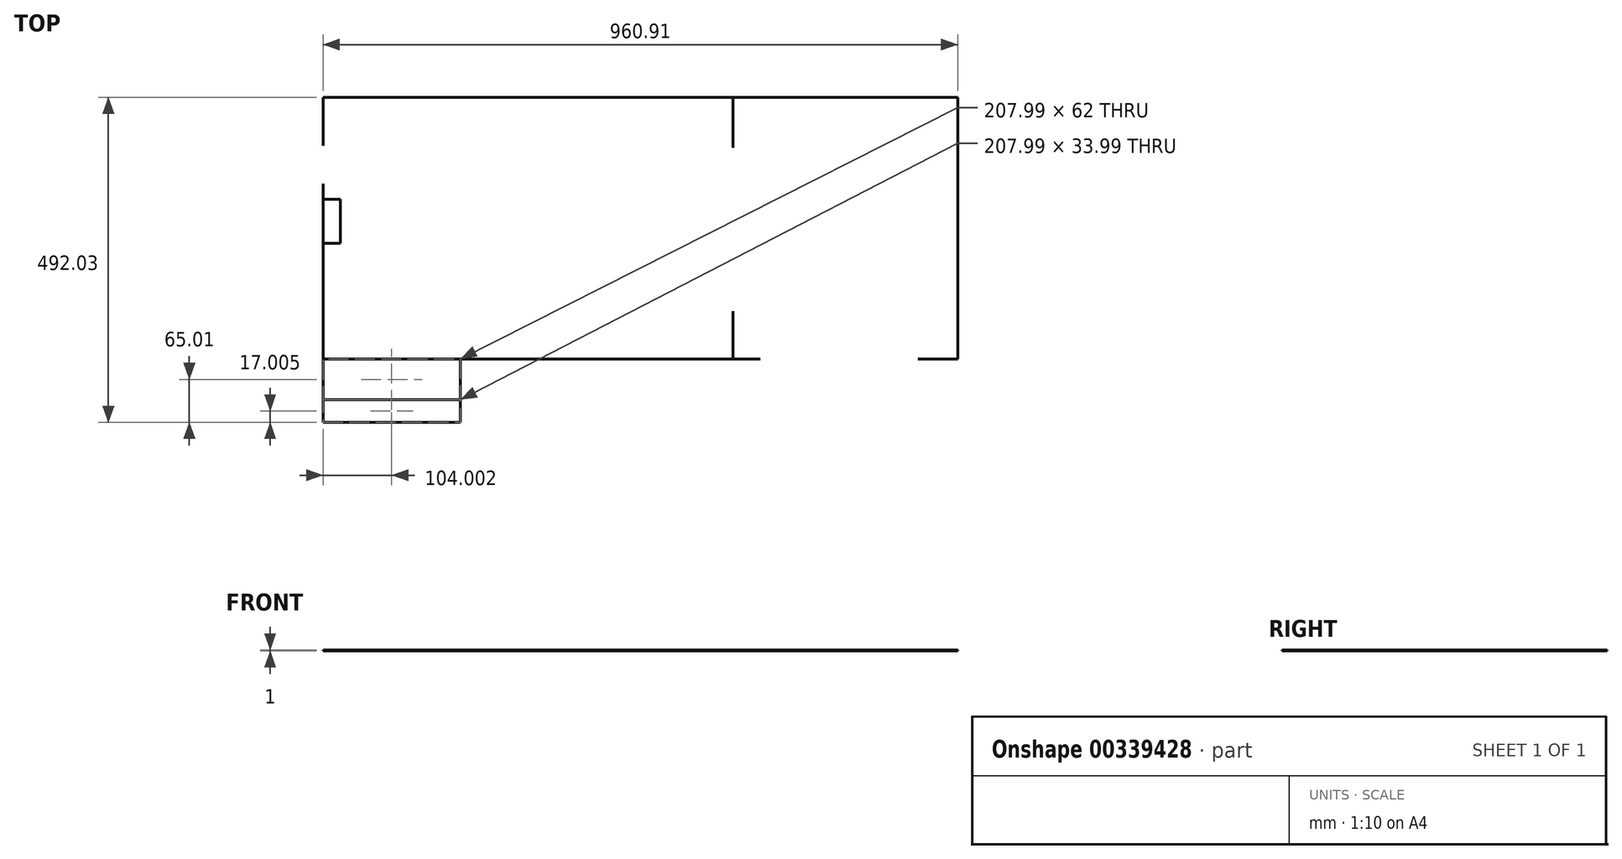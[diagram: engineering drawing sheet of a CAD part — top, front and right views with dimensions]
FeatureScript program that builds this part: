
annotation { "Feature Type Name" : "Feature", "Feature Type Description" : "" }
export const myFeature = defineFeature(function(context is Context, id is Id, definition is map)
    precondition{}
    {
        {
            var Q0;
            Q0=qCreatedBy(makeId("Top.planeOp"),FACE);
            var sketch = newSketch(context, id + "F0", { "sketchPlane" : qUnion([Q0])});
            skLineSegment(sketch, "E0.bottom", {"start": v(104.12, 1.02) * mm, "end": v(-308.77, 1.02) * mm});
            skLineSegment(sketch, "E1.0", {"start": v(104.13, 1.02) * mm, "end": v(104.13, 73.02) * mm});
            skLineSegment(sketch, "E2.0", {"start": v(104.13, 1) * mm, "end": v(-308.77, 1) * mm});
            skLineSegment(sketch, "E3.trimOffspring", {"start": v(-308.77, 1) * mm, "end": v(-308.77, -95) * mm});
            skLineSegment(sketch, "E4", {"start": v(-308.77, -95) * mm, "end": v(-308.78, -95) * mm});
            skLineSegment(sketch, "E5", {"start": v(104.12, 73.02) * mm, "end": v(104.13, 73.02) * mm});
            skLineSegment(sketch, "E6", {"start": v(104.12, 321.02) * mm, "end": v(104.13, 321.02) * mm});
            skLineSegment(sketch, "E7.trimOffspring", {"start": v(104.13, 321.02) * mm, "end": v(104.13, 397.02) * mm});
            skLineSegment(sketch, "E8.trimOffspring", {"start": v(104.12, 321.02) * mm, "end": v(104.12, 397.02) * mm});
            skLineSegment(sketch, "E9.trimOffspring", {"start": v(104.12, 1.02) * mm, "end": v(104.12, 73.02) * mm});
            skLineSegment(sketch, "E10", {"start": v(104.13, 1.02) * mm, "end": v(145.13, 1.02) * mm});
            skLineSegment(sketch, "E11", {"start": v(104.13, 1) * mm, "end": v(145.13, 1) * mm});
            skLineSegment(sketch, "E12", {"start": v(145.13, 1.02) * mm, "end": v(145.13, 1) * mm});
            skPoint(sketch, "E13.orphan", {"position": v(58.62, 0) * mm});
            skLineSegment(sketch, "E14", {"start": v(-346.77, 329) * mm, "end": v(-346.76, 329) * mm});
            skLineSegment(sketch, "E15", {"start": v(-345.78, 256) * mm, "end": v(-345.77, 256) * mm});
            skLineSegment(sketch, "E16", {"start": v(-516.78, 397.03) * mm, "end": v(-516.78, 324.02) * mm});
            skLineSegment(sketch, "E17.0", {"start": v(-516.77, 397.02) * mm, "end": v(-516.77, 324.02) * mm});
            skLineSegment(sketch, "E18", {"start": v(-516.78, 324.02) * mm, "end": v(-516.77, 324.02) * mm});
            skLineSegment(sketch, "E19", {"start": v(-516.78, 240.87) * mm, "end": v(-516.78, 240.87) * mm});
            skLineSegment(sketch, "E20", {"start": v(-516.77, 243.02) * mm, "end": v(-490.78, 243.02) * mm});
            skLineSegment(sketch, "E21", {"start": v(-490.78, 243.02) * mm, "end": v(-490.78, 176.02) * mm});
            skLineSegment(sketch, "E22", {"start": v(104.13, 397.02) * mm, "end": v(444.12, 397.02) * mm});
            skLineSegment(sketch, "E23.0", {"start": v(444.12, 1.02) * mm, "end": v(444.12, 397.02) * mm});
            skLineSegment(sketch, "E24", {"start": v(384.13, 1) * mm, "end": v(444.13, 1) * mm});
            skLineSegment(sketch, "E25.0", {"start": v(384.13, 1.02) * mm, "end": v(444.12, 1.02) * mm});
            skLineSegment(sketch, "E26", {"start": v(384.13, 1.02) * mm, "end": v(384.13, 1) * mm});
            skPoint(sketch, "E27.orphan", {"position": v(341.53, 1) * mm});
            skLineSegment(sketch, "E28.trimOffspring", {"start": v(444.13, 1) * mm, "end": v(444.13, 397.03) * mm});
            skLineSegment(sketch, "E29", {"start": v(-308.77, -95) * mm, "end": v(-516.78, -95) * mm});
            skLineSegment(sketch, "E30.0", {"start": v(-308.78, -95) * mm, "end": v(-516.77, -95) * mm});
            skLineSegment(sketch, "E31", {"start": v(-490.78, 176.02) * mm, "end": v(-516.77, 176.02) * mm});
            skLineSegment(sketch, "E32.trimOffspring", {"start": v(-308.78, 1) * mm, "end": v(-308.78, -61) * mm});
            skLineSegment(sketch, "E33.trimOffspring", {"start": v(-308.78, 1.02) * mm, "end": v(-516.77, 1.02) * mm});
            skLineSegment(sketch, "E34.trimOffspring", {"start": v(-308.78, 1) * mm, "end": v(-516.77, 1) * mm});
            skLineSegment(sketch, "E35", {"start": v(-308.78, 1.02) * mm, "end": v(-308.77, 1.02) * mm});
            skLineSegment(sketch, "E36", {"start": v(-516.77, 176.02) * mm, "end": v(-516.77, 1.02) * mm});
            skLineSegment(sketch, "E37", {"start": v(-516.77, -61) * mm, "end": v(-308.78, -61) * mm});
            skLineSegment(sketch, "E38.trimOffspring", {"start": v(-308.78, -61) * mm, "end": v(-308.78, -95) * mm});
            skLineSegment(sketch, "E39.trimOffspring", {"start": v(-516.77, -61) * mm, "end": v(-516.77, -95) * mm});
            skLineSegment(sketch, "E40.trimOffspring", {"start": v(-516.77, 1) * mm, "end": v(-516.77, -61) * mm});
            skPoint(sketch, "E41.orphan", {"position": v(-515.78, 256.02) * mm});
            skLineSegment(sketch, "E42", {"start": v(-516.77, 266) * mm, "end": v(-516.77, 243.02) * mm});
            skLineSegment(sketch, "E43.trimOffspring", {"start": v(-516.78, 266) * mm, "end": v(-516.78, -95) * mm});
            skLineSegment(sketch, "E44", {"start": v(-516.78, 266) * mm, "end": v(-516.77, 266) * mm});
            skLineSegment(sketch, "E45", {"start": v(-516.78, 397.03) * mm, "end": v(444.13, 397.03) * mm});
            skLineSegment(sketch, "E46", {"start": v(-516.77, 397.02) * mm, "end": v(104.12, 397.02) * mm});
            skSolve(sketch);
        }
        {
            var Q0;
            Q0 = qSketchRegion(id + "F0", true);
            extrude(context, id + "F1", {"entities" : qUnion([Q0]), "depth" : 1 * mm});
        }
    });
